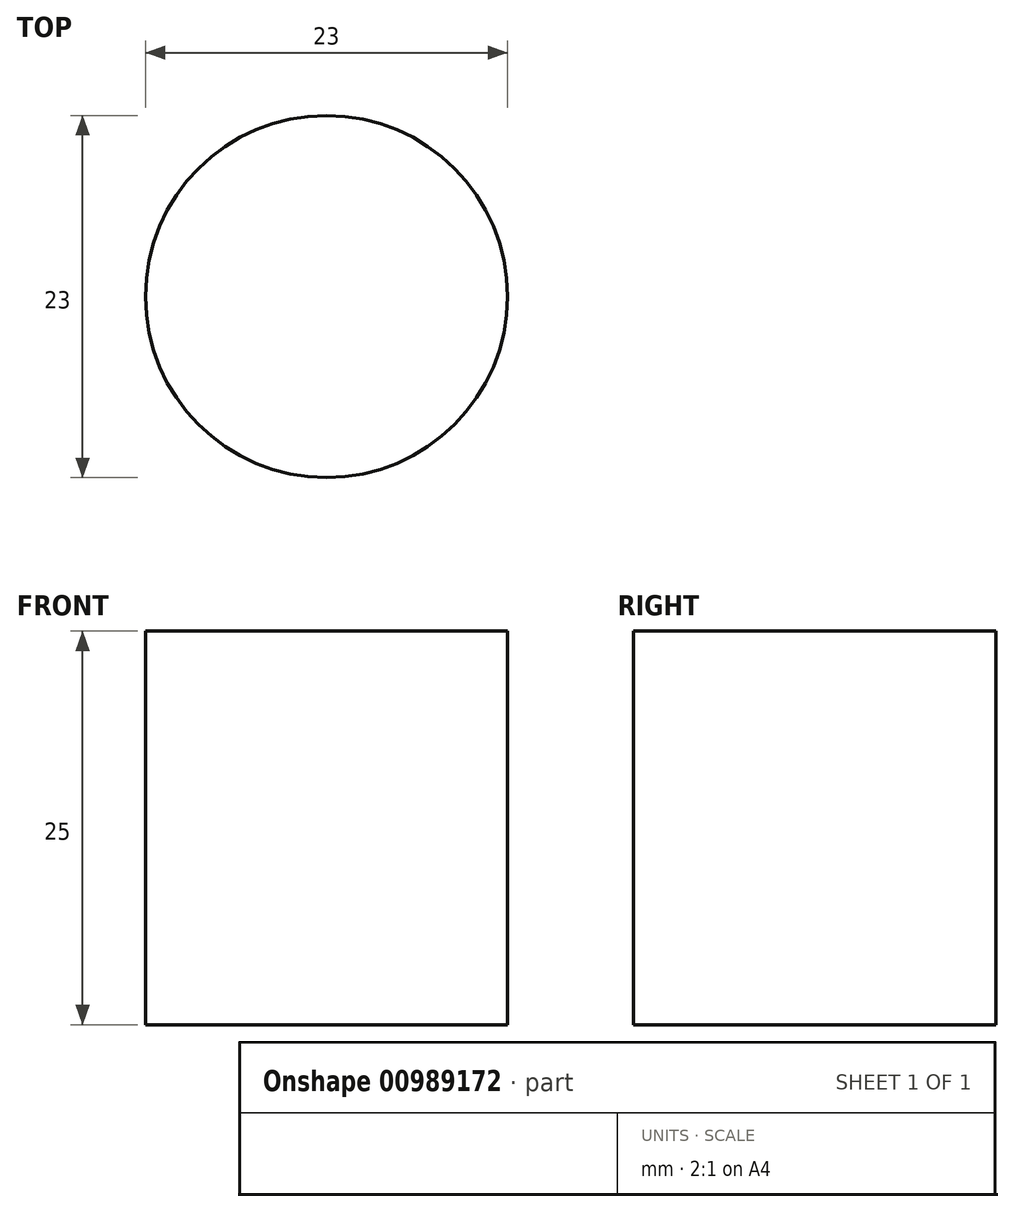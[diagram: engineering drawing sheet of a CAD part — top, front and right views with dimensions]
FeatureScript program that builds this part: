
annotation { "Feature Type Name" : "Feature", "Feature Type Description" : "" }
export const myFeature = defineFeature(function(context is Context, id is Id, definition is map)
    precondition{}
    {
        {
            var Q0;
            Q0=qCreatedBy(makeId("Front.planeOp"),FACE);
            var sketch = newSketch(context, id + "F0", { "sketchPlane" : qUnion([Q0])});
            skLineSegment(sketch, "E0", {"start": v(0, 0) * mm, "end": v(0, 10) * mm});
            skLineSegment(sketch, "E1", {"start": v(0, 10) * mm, "end": v(15, 10) * mm});
            skLineSegment(sketch, "E2", {"start": v(15, 10) * mm, "end": v(15, 0) * mm});
            skLineSegment(sketch, "E3", {"start": v(15, 0) * mm, "end": v(0, 0) * mm});
            skLineSegment(sketch, "E4", {"start": v(11.5, 10) * mm, "end": v(11.5, 50) * mm});
            skLineSegment(sketch, "E5", {"start": v(0, 10) * mm, "end": v(0, 50) * mm});
            skLineSegment(sketch, "E6", {"start": v(0, 50) * mm, "end": v(11.5, 50) * mm});
            skSolve(sketch);
        }
        {
            var Q0;
            {var subQ2=sQuery(id+"F0.wireOp",EDGE,"E4");Q0=makeQuery(id+"F0.imprint","IMPRINT",FACE,{"disambiguationData":[TD([[makeQuery(id+"F0.imprint","IMPRINT",EDGE,{"derivedFrom":subQ2}),1.0]])]});}
            var Q1;
            {var subQ3=sQuery(id+"F0.wireOp",EDGE,"E0");Q1=makeQuery(id+"F0.imprint","IMPRINT",FACE,{"disambiguationData":[TD([[makeQuery(id+"F0.imprint","IMPRINT",EDGE,{"derivedFrom":subQ3}),-1.0]])]});}
            var Q2;
            Q2=sQuery(id+"F0.wireOp",EDGE,"E4");
            var Q3;
            Q3=sQuery(id+"F0.wireOp",EDGE,"E5");
            revolve(context, id + "F1", {"surfaceOperationType" : NewSurfaceOperationType.NEW, "entities" : qUnion([Q0, Q1]), "surfaceEntities" : qUnion([Q2]), "axis" : qUnion([Q3]), "revolveType" : RevolveType.ONE_DIRECTION, "angle" : 360 * degree});
        }
        {
            var Q0;
            Q0=qCreatedBy(makeId("Front.planeOp"),FACE);
            var sketch = newSketch(context, id + "F2", { "sketchPlane" : qUnion([Q0])});
            skLineSegment(sketch, "E7", {"start": v(11.43, 50.05) * mm, "end": v(0, 32.56) * mm});
            skLineSegment(sketch, "E8", {"start": v(0, 32.56) * mm, "end": v(0, 0) * mm});
            skLineSegment(sketch, "E9", {"start": v(0, 0) * mm, "end": v(0, 32.56) * mm});
            skLineSegment(sketch, "E10", {"start": v(11.43, 50.05) * mm, "end": v(8.56, 50.05) * mm});
            skLineSegment(sketch, "E11", {"start": v(8.56, 50.05) * mm, "end": v(0, 36.95) * mm, "construction": true});
            skSolve(sketch);
        }
        {
            var Q0;
            Q0=makeQuery(id+"F1.opRevolve","SWEPT_FACE",FACE,{"disambiguationData":[OSD([sQuery(id+"F0.wireOp",EDGE,"E6")])]});
            var Q1;
            Q1=makeQuery(id+"F1.opRevolve","SWEPT_FACE",FACE,{"disambiguationData":[OSD([sQuery(id+"F0.wireOp",EDGE,"E1")])]});
            var Q2;
            Q2=makeQuery(id+"F1.opRevolve","SWEPT_FACE",FACE,{"disambiguationData":[OSD([sQuery(id+"F0.wireOp",EDGE,"E3")])]});
            var Q3;
            Q3=sQuery(id+"F2.wireOp",EDGE,"E7");
            var Q4;
            Q4=sQuery(id+"F2.wireOp",EDGE,"E10");
            extrude(context, id + "F3", {"entities" : qUnion([Q0, Q1, Q2]), "operationType" : NewBodyOperationType.REMOVE, "surfaceEntities" : qUnion([Q3, Q4]), "oppositeDirection" : true, "depth" : 25 * mm, "offsetDistance" : 25 * mm});
        }
    });
